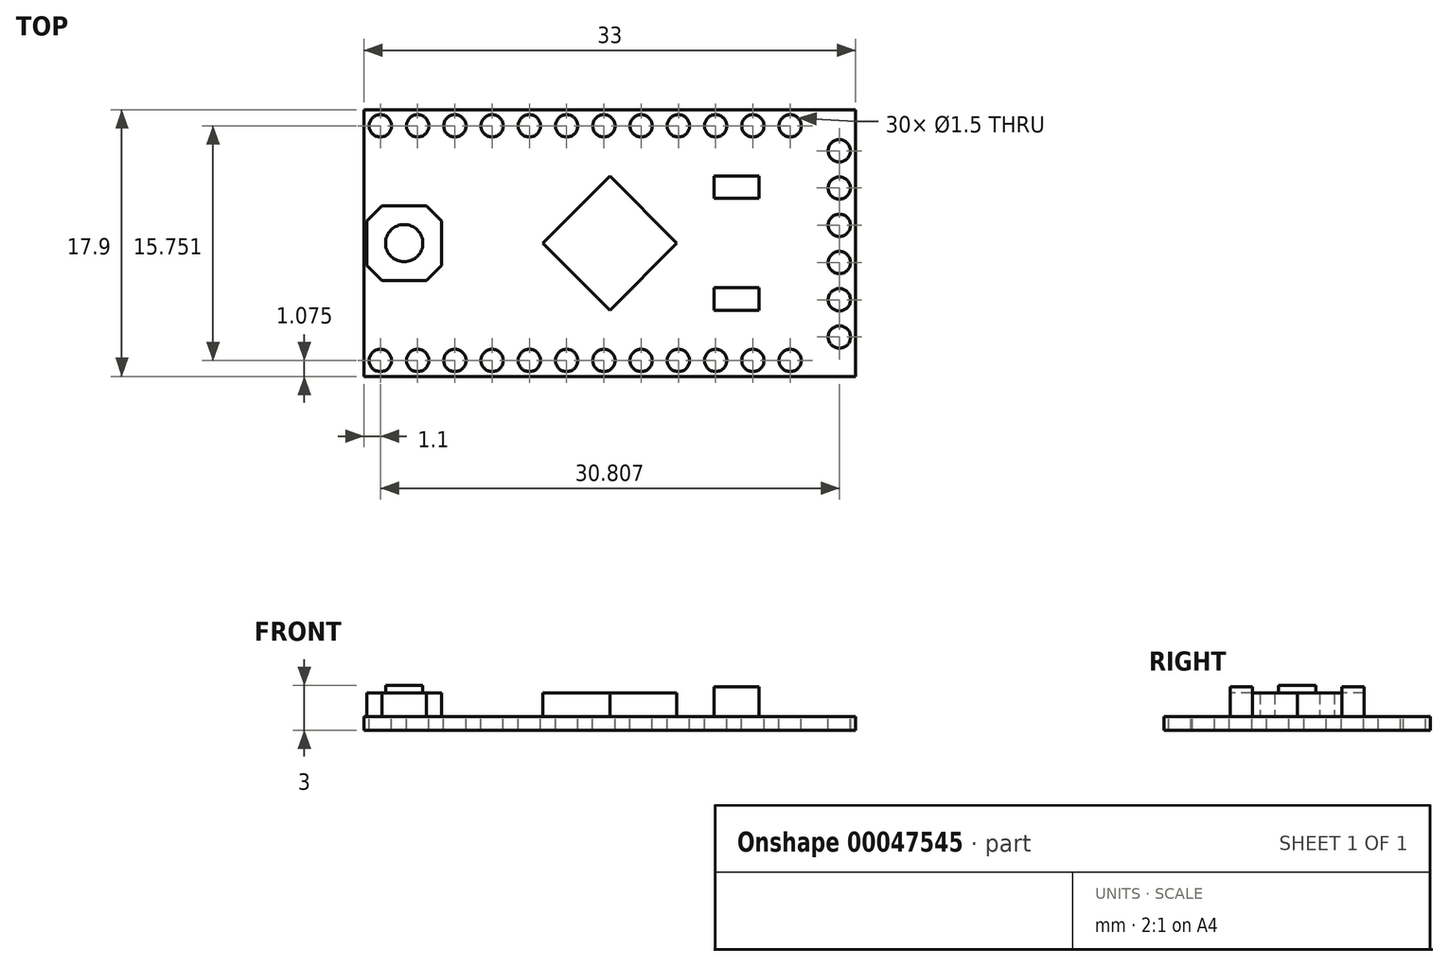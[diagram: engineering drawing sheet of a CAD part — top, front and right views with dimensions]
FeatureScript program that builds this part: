
annotation { "Feature Type Name" : "Feature", "Feature Type Description" : "" }
export const myFeature = defineFeature(function(context is Context, id is Id, definition is map)
    precondition{}
    {
        {
            var Q0;
            Q0=qCreatedBy(makeId("Top.planeOp"),FACE);
            var sketch = newSketch(context, id + "F0", { "sketchPlane" : qUnion([Q0])});
            skLineSegment(sketch, "E0.bottom", {"start": v(-16.5, 8.95) * mm, "end": v(16.5, 8.95) * mm});
            skLineSegment(sketch, "E0.top", {"start": v(-16.5, -8.95) * mm, "end": v(16.5, -8.95) * mm});
            skLineSegment(sketch, "E0.left", {"start": v(-16.5, 8.95) * mm, "end": v(-16.5, -8.95) * mm});
            skLineSegment(sketch, "E0.right", {"start": v(16.5, 8.95) * mm, "end": v(16.5, -8.95) * mm});
            skSolve(sketch);
        }
        {
            var Q0;
            Q0 = qSketchRegion(id + "F0", true);
            extrude(context, id + "F1", {"entities" : qUnion([Q0]), "depth" : .9 * mm});
        }
        {
            var Q0;
            Q0=makeQuery(id+"F1.opExtrude","CAP_FACE",FACE,{"disambiguationData":[OSD([sQuery(id+"F0.wireOp",EDGE,"E0.bottom"),sQuery(id+"F0.wireOp",EDGE,"E0.top"),sQuery(id+"F0.wireOp",EDGE,"E0.left"),sQuery(id+"F0.wireOp",EDGE,"E0.right")])],"isStart":false});
            var sketch = newSketch(context, id + "F2", { "sketchPlane" : qUnion([Q0])});
            skLineSegment(sketch, "E1", {"start": v(0, 4.5) * mm, "end": v(4.5, 0) * mm});
            skLineSegment(sketch, "E2", {"start": v(4.5, 0) * mm, "end": v(0, -4.5) * mm});
            skLineSegment(sketch, "E3", {"start": v(0, -4.5) * mm, "end": v(-4.5, 0) * mm});
            skLineSegment(sketch, "E4", {"start": v(-4.5, 0) * mm, "end": v(0, 4.5) * mm});
            skSolve(sketch);
        }
        {
            var Q0;
            Q0 = qSketchRegion(id + "F2", true);
            extrude(context, id + "F3", {"entities" : qUnion([Q0]), "operationType" : NewBodyOperationType.ADD, "depth" : 1.6 * mm});
        }
        {
            var Q0;
            Q0=makeQuery(id+"F1.opExtrude","CAP_FACE",FACE,{"disambiguationData":[OSD([sQuery(id+"F0.wireOp",EDGE,"E0.bottom"),sQuery(id+"F0.wireOp",EDGE,"E0.top"),sQuery(id+"F0.wireOp",EDGE,"E0.left"),sQuery(id+"F0.wireOp",EDGE,"E0.right")])],"isStart":false});
            var sketch = newSketch(context, id + "F4", { "sketchPlane" : qUnion([Q0])});
            skLineSegment(sketch, "E5.bottom", {"start": v(-15.3, 2.5) * mm, "end": v(-12.3, 2.5) * mm});
            skLineSegment(sketch, "E5.top", {"start": v(-15.3, -2.5) * mm, "end": v(-12.3, -2.5) * mm});
            skLineSegment(sketch, "E5.left", {"start": v(-16.3, 1.5) * mm, "end": v(-16.3, -1.5) * mm});
            skLineSegment(sketch, "E5.right", {"start": v(-11.3, 1.5) * mm, "end": v(-11.3, -1.5) * mm});
            skLineSegment(sketch, "E6", {"start": v(-12.3, 2.5) * mm, "end": v(-11.3, 1.5) * mm});
            skLineSegment(sketch, "E7", {"start": v(-11.3, -1.5) * mm, "end": v(-12.3, -2.5) * mm});
            skLineSegment(sketch, "E8", {"start": v(-16.3, -1.5) * mm, "end": v(-15.3, -2.5) * mm});
            skLineSegment(sketch, "E9", {"start": v(-15.3, 2.5) * mm, "end": v(-16.3, 1.5) * mm});
            skPoint(sketch, "E10.orphan", {"position": v(-11.3, 2.5) * mm});
            skSolve(sketch);
        }
        {
            var Q0;
            Q0 = qSketchRegion(id + "F4", true);
            extrude(context, id + "F5", {"entities" : qUnion([Q0]), "operationType" : NewBodyOperationType.ADD, "depth" : 1.6 * mm});
        }
        {
            var Q0;
            Q0=makeQuery(id+"F5.opExtrude","CAP_FACE",FACE,{"disambiguationData":[OSD([sQuery(id+"F4.wireOp",EDGE,"E5.bottom"),sQuery(id+"F4.wireOp",EDGE,"E5.top"),sQuery(id+"F4.wireOp",EDGE,"E5.left"),sQuery(id+"F4.wireOp",EDGE,"E5.right"),sQuery(id+"F4.wireOp",EDGE,"E6"),sQuery(id+"F4.wireOp",EDGE,"E7"),sQuery(id+"F4.wireOp",EDGE,"E8"),sQuery(id+"F4.wireOp",EDGE,"E9")])],"isStart":false});
            var sketch = newSketch(context, id + "F6", { "sketchPlane" : qUnion([Q0])});
            skCircle(sketch, "E11", {"center": v(-13.8, 0) * mm, "radius": 1.25 * mm});
            skPoint(sketch, "E11.centerSnap0", {"position": v(-13.8, 2.5) * mm});
            skSolve(sketch);
        }
        {
            var Q0;
            Q0 = qSketchRegion(id + "F6", true);
            extrude(context, id + "F7", {"entities" : qUnion([Q0]), "operationType" : NewBodyOperationType.ADD, "depth" : .5 * mm});
        }
        {
            var Q0;
            Q0=makeQuery(id+"F1.opExtrude","CAP_FACE",FACE,{"disambiguationData":[OSD([sQuery(id+"F0.wireOp",EDGE,"E0.bottom"),sQuery(id+"F0.wireOp",EDGE,"E0.top"),sQuery(id+"F0.wireOp",EDGE,"E0.left"),sQuery(id+"F0.wireOp",EDGE,"E0.right")])],"isStart":false});
            var sketch = newSketch(context, id + "F8", { "sketchPlane" : qUnion([Q0])});
            skCircle(sketch, "E12", {"center": v(-15.4, 7.88) * mm, "radius": 0.75 * mm});
            skCircle(sketch, "E13.1.0.0", {"center": v(-12.9, 7.88) * mm, "radius": 0.75 * mm});
            skCircle(sketch, "E13.2.0.0", {"center": v(-10.4, 7.88) * mm, "radius": 0.75 * mm});
            skCircle(sketch, "E13.3.0.0", {"center": v(-7.9, 7.88) * mm, "radius": 0.75 * mm});
            skCircle(sketch, "E13.4.0.0", {"center": v(-5.4, 7.88) * mm, "radius": 0.75 * mm});
            skCircle(sketch, "E13.5.0.0", {"center": v(-2.9, 7.88) * mm, "radius": 0.75 * mm});
            skCircle(sketch, "E13.6.0.0", {"center": v(-0.4, 7.88) * mm, "radius": 0.75 * mm});
            skCircle(sketch, "E13.7.0.0", {"center": v(2.1, 7.88) * mm, "radius": 0.75 * mm});
            skCircle(sketch, "E13.8.0.0", {"center": v(4.6, 7.88) * mm, "radius": 0.75 * mm});
            skCircle(sketch, "E13.9.0.0", {"center": v(7.1, 7.88) * mm, "radius": 0.75 * mm});
            skCircle(sketch, "E13.10.0.0", {"center": v(9.6, 7.88) * mm, "radius": 0.75 * mm});
            skCircle(sketch, "E13.11.0.0", {"center": v(12.1, 7.88) * mm, "radius": 0.75 * mm});
            skLineSegment(sketch, "E13.direction1", {"start": v(-15.4, 7.88) * mm, "end": v(-12.9, 7.88) * mm, "construction": true});
            skPoint(sketch, "E14.endSnap0", {"position": v(16.5, 0) * mm});
            skCircle(sketch, "E15.MirrorC", {"center": v(-12.9, -7.88) * mm, "radius": 0.75 * mm});
            skCircle(sketch, "E16.MirrorC", {"center": v(-5.4, -7.88) * mm, "radius": 0.75 * mm});
            skCircle(sketch, "E17.MirrorC", {"center": v(-15.4, -7.88) * mm, "radius": 0.75 * mm});
            skCircle(sketch, "E18.MirrorC", {"center": v(-10.4, -7.88) * mm, "radius": 0.75 * mm});
            skCircle(sketch, "E19.MirrorC", {"center": v(-7.9, -7.88) * mm, "radius": 0.75 * mm});
            skCircle(sketch, "E20.MirrorC", {"center": v(12.1, -7.88) * mm, "radius": 0.75 * mm});
            skCircle(sketch, "E21.MirrorC", {"center": v(-2.9, -7.88) * mm, "radius": 0.75 * mm});
            skCircle(sketch, "E22.MirrorC", {"center": v(-0.4, -7.88) * mm, "radius": 0.75 * mm});
            skCircle(sketch, "E23.MirrorC", {"center": v(2.1, -7.88) * mm, "radius": 0.75 * mm});
            skCircle(sketch, "E24.MirrorC", {"center": v(4.6, -7.88) * mm, "radius": 0.75 * mm});
            skCircle(sketch, "E25.MirrorC", {"center": v(7.1, -7.88) * mm, "radius": 0.75 * mm});
            skCircle(sketch, "E26.MirrorC", {"center": v(9.6, -7.88) * mm, "radius": 0.75 * mm});
            skLineSegment(sketch, "E27.MirrorCS", {"start": v(-15.4, -7.88) * mm, "end": v(-12.9, -7.88) * mm, "construction": true});
            skCircle(sketch, "E28", {"center": v(15.4, 6.2) * mm, "radius": 0.75 * mm});
            skCircle(sketch, "E29.1.0.0", {"center": v(15.4, 3.7) * mm, "radius": 0.75 * mm});
            skCircle(sketch, "E29.2.0.0", {"center": v(15.4, 1.2) * mm, "radius": 0.75 * mm});
            skCircle(sketch, "E29.3.0.0", {"center": v(15.4, -1.3) * mm, "radius": 0.75 * mm});
            skCircle(sketch, "E29.4.0.0", {"center": v(15.4, -3.8) * mm, "radius": 0.75 * mm});
            skCircle(sketch, "E29.5.0.0", {"center": v(15.4, -6.3) * mm, "radius": 0.75 * mm});
            skLineSegment(sketch, "E29.direction1", {"start": v(15.4, 6.2) * mm, "end": v(15.4, 3.7) * mm, "construction": true});
            skSolve(sketch);
        }
        {
            var Q0;
            Q0 = qSketchRegion(id + "F8", true);
            extrude(context, id + "F9", {"entities" : qUnion([Q0]), "operationType" : NewBodyOperationType.REMOVE, "oppositeDirection" : true, "depth" : 25 * mm});
        }
        {
            var Q0;
            Q0=makeQuery(id+"F1.opExtrude","CAP_FACE",FACE,{"disambiguationData":[OSD([sQuery(id+"F0.wireOp",EDGE,"E0.bottom"),sQuery(id+"F0.wireOp",EDGE,"E0.top"),sQuery(id+"F0.wireOp",EDGE,"E0.left"),sQuery(id+"F0.wireOp",EDGE,"E0.right")])],"isStart":false});
            var sketch = newSketch(context, id + "F10", { "sketchPlane" : qUnion([Q0])});
            skLineSegment(sketch, "E30.bottom", {"start": v(7, 4.5) * mm, "end": v(10, 4.5) * mm});
            skLineSegment(sketch, "E30.top", {"start": v(7, 3) * mm, "end": v(10, 3) * mm});
            skLineSegment(sketch, "E30.left", {"start": v(7, 4.5) * mm, "end": v(7, 3) * mm});
            skLineSegment(sketch, "E30.right", {"start": v(10, 4.5) * mm, "end": v(10, 3) * mm});
            skLineSegment(sketch, "E31.bottom", {"start": v(7, -3) * mm, "end": v(10, -3) * mm});
            skLineSegment(sketch, "E31.top", {"start": v(7, -4.5) * mm, "end": v(10, -4.5) * mm});
            skLineSegment(sketch, "E31.left", {"start": v(7, -3) * mm, "end": v(7, -4.5) * mm});
            skLineSegment(sketch, "E31.right", {"start": v(10, -3) * mm, "end": v(10, -4.5) * mm});
            skSolve(sketch);
        }
        {
            var Q0;
            Q0 = qSketchRegion(id + "F10", true);
            extrude(context, id + "F11", {"entities" : qUnion([Q0]), "operationType" : NewBodyOperationType.ADD, "depth" : 2 * mm});
        }
    });
